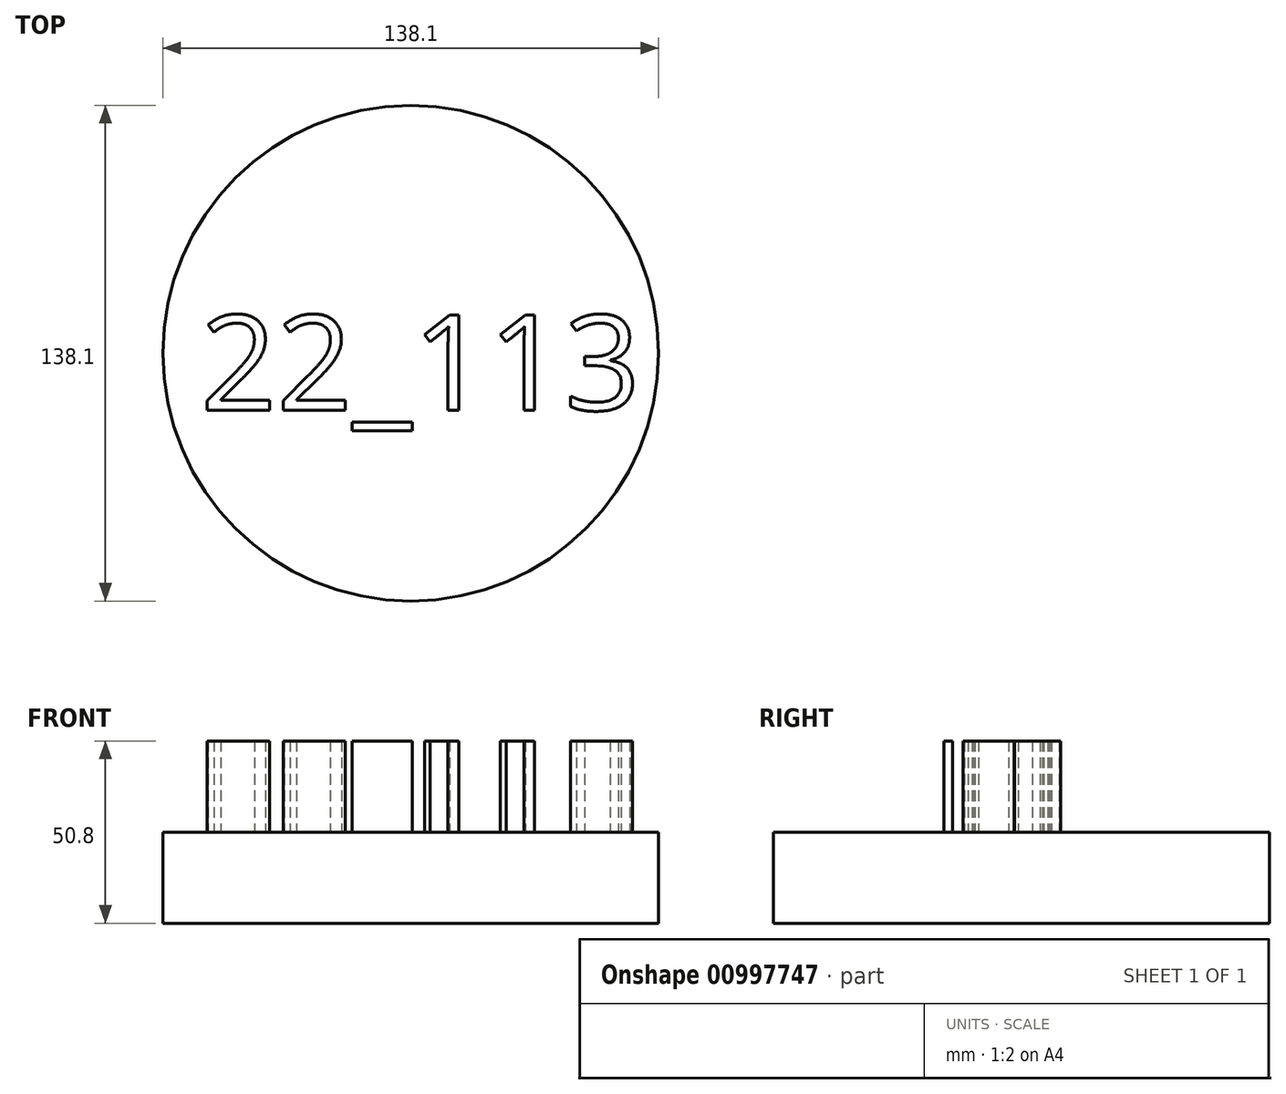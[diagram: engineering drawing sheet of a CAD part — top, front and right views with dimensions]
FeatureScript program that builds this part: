
annotation { "Feature Type Name" : "Feature", "Feature Type Description" : "" }
export const myFeature = defineFeature(function(context is Context, id is Id, definition is map)
    precondition{}
    {
        {
            var Q0;
            Q0=qCreatedBy(makeId("Top.planeOp"),FACE);
            var sketch = newSketch(context, id + "F0", { "sketchPlane" : qUnion([Q0])});
            skCircle(sketch, "E0", {"center": v(0, 0) * mm, "radius": 69.05 * mm});
            skSolve(sketch);
        }
        {
            var Q0;
            Q0 = qSketchRegion(id + "F0", true);
            extrude(context, id + "F1", {"entities" : qUnion([Q0]), "depth" : 25.4 * mm, "offsetDistance" : 25.4 * mm});
        }
        {
            var Q0;
            Q0=makeQuery(id+"F1.opExtrude","CAP_FACE",FACE,{"disambiguationData":[OSD([sQuery(id+"F0.wireOp",EDGE,"E0")])],"isStart":false});
            var sketch = newSketch(context, id + "F2", { "sketchPlane" : qUnion([Q0])});
            skText(sketch, "E1", { "text": "22_113", "fontName": "OpenSans-Regular.ttf"});
            const initialGuessF2  = {"E1": [-0.05855, -0.01586, 1, 0, 0.02667]};
            skSetInitialGuess(sketch, initialGuessF2);
            skSolve(sketch);
        }
        {
            var Q0;
            Q0 = qSketchRegion(id + "F2", true);
            extrude(context, id + "F3", {"entities" : qUnion([Q0]), "operationType" : NewBodyOperationType.ADD, "depth" : 25.4 * mm, "offsetDistance" : 25.4 * mm});
        }
    });
